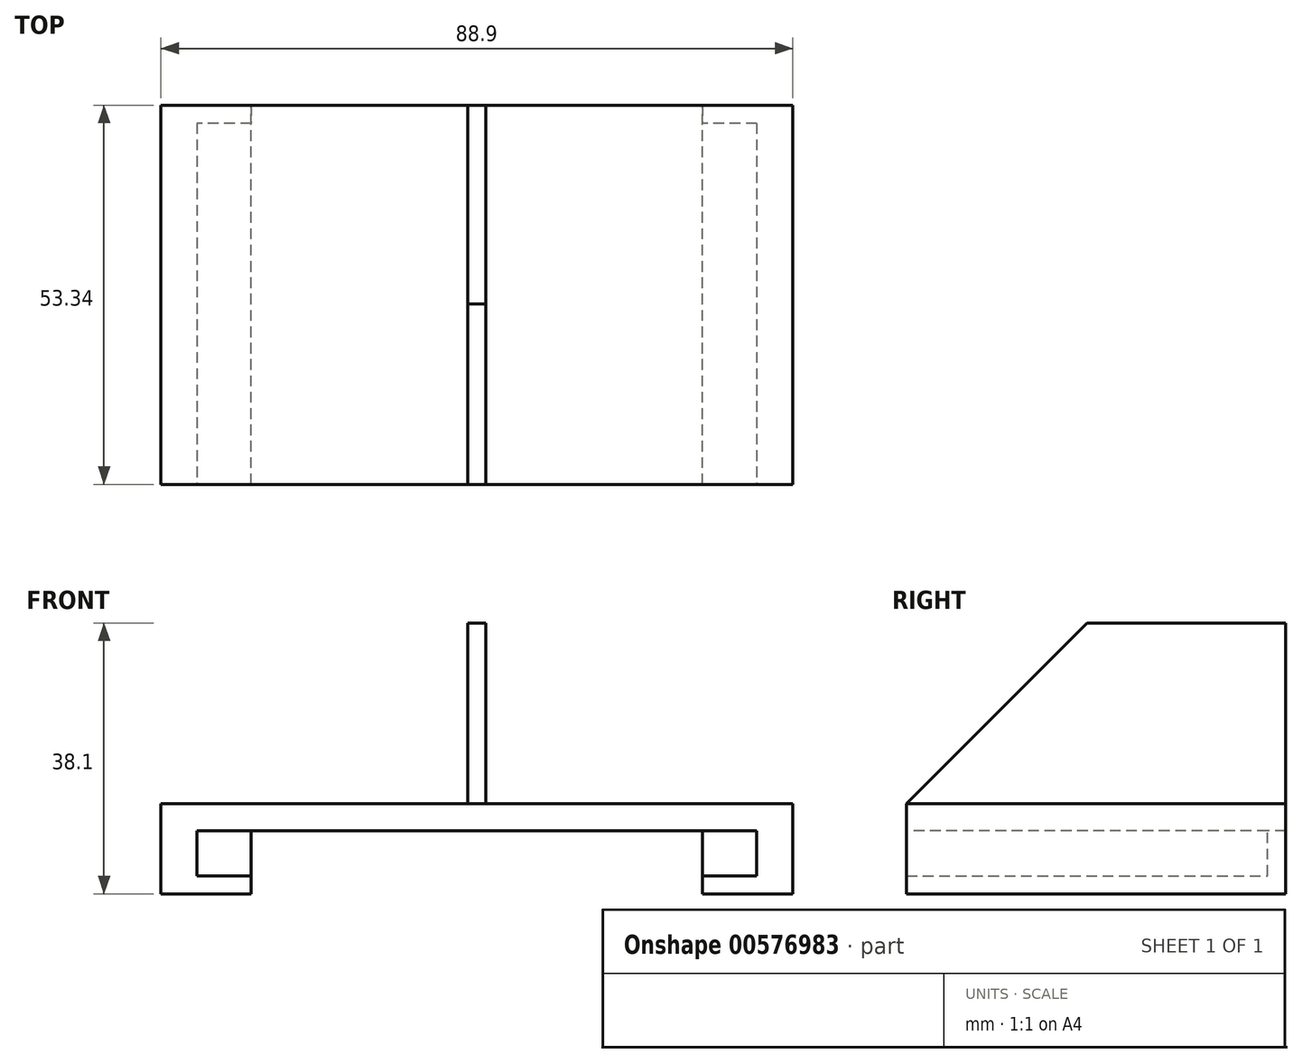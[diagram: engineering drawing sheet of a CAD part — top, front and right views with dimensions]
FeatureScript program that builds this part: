
annotation { "Feature Type Name" : "Feature", "Feature Type Description" : "" }
export const myFeature = defineFeature(function(context is Context, id is Id, definition is map)
    precondition{}
    {
        {
            var Q0;
            Q0=qCreatedBy(makeId("Top.planeOp"),FACE);
            var sketch = newSketch(context, id + "F0", { "sketchPlane" : qUnion([Q0])});
            skLineSegment(sketch, "E0.bottom", {"start": v(44.45, -26.67) * mm, "end": v(-44.45, -26.67) * mm});
            skLineSegment(sketch, "E0.top", {"start": v(44.45, 26.67) * mm, "end": v(-44.45, 26.67) * mm});
            skLineSegment(sketch, "E0.left", {"start": v(44.45, -26.67) * mm, "end": v(44.45, 26.67) * mm});
            skLineSegment(sketch, "E0.right", {"start": v(-44.45, -26.67) * mm, "end": v(-44.45, 26.67) * mm});
            skPoint(sketch, "E0.middle", {"position": v(0, 0) * mm});
            skSolve(sketch);
        }
        {
            var Q0;
            Q0=makeQuery(id+"F0.imprint","IMPRINT",FACE,{"disambiguationData":[TD([[makeQuery(id+"F0.imprint","IMPRINT",EDGE,{"derivedFrom":sQuery(id+"F0.wireOp",EDGE,"E0.bottom")}),-1.0]])]});
            extrude(context, id + "F1", {"entities" : qUnion([Q0]), "depth" : 12.7 * mm, "offsetDistance" : 25.4 * mm});
        }
        {
            var Q0;
            Q0=makeQuery(id+"F1.opExtrude","SWEPT_FACE",FACE,{"disambiguationData":[OSD([sQuery(id+"F0.wireOp",EDGE,"E0.bottom")])]});
            var sketch = newSketch(context, id + "F2", { "sketchPlane" : qUnion([Q0])});
            skLineSegment(sketch, "E1.bottom", {"start": v(39.37, 2.54) * mm, "end": v(-39.37, 2.54) * mm});
            skLineSegment(sketch, "E1.top", {"start": v(39.37, 8.9) * mm, "end": v(-39.37, 8.9) * mm});
            skLineSegment(sketch, "E1.left", {"start": v(39.37, 2.54) * mm, "end": v(39.37, 8.9) * mm});
            skLineSegment(sketch, "E1.right", {"start": v(-39.37, 2.54) * mm, "end": v(-39.37, 8.9) * mm});
            skPoint(sketch, "E1.middle", {"position": v(0, 5.72) * mm});
            skSolve(sketch);
        }
        {
            var Q0;
            Q0=makeQuery(id+"F2.imprint","IMPRINT",FACE,{"disambiguationData":[TD([[makeQuery(id+"F2.imprint","IMPRINT",EDGE,{"derivedFrom":sQuery(id+"F2.wireOp",EDGE,"E1.bottom")}),-1.0]])]});
            extrude(context, id + "F3", {"entities" : qUnion([Q0]), "operationType" : NewBodyOperationType.REMOVE, "oppositeDirection" : true, "depth" : 50.8 * mm, "offsetDistance" : 25.4 * mm});
        }
        {
            var Q0;
            Q0=makeQuery(id+"F1.opExtrude","SWEPT_FACE",FACE,{"disambiguationData":[OSD([sQuery(id+"F0.wireOp",EDGE,"E0.bottom")])]});
            var sketch = newSketch(context, id + "F4", { "sketchPlane" : qUnion([Q0])});
            skLineSegment(sketch, "E2.bottom", {"start": v(31.75, -8.9) * mm, "end": v(-31.75, -8.9) * mm});
            skLineSegment(sketch, "E2.top", {"start": v(31.75, 8.9) * mm, "end": v(-31.75, 8.9) * mm});
            skLineSegment(sketch, "E2.left", {"start": v(31.75, -8.9) * mm, "end": v(31.75, 8.9) * mm});
            skLineSegment(sketch, "E2.right", {"start": v(-31.75, -8.9) * mm, "end": v(-31.75, 8.9) * mm});
            skPoint(sketch, "E2.middle", {"position": v(0, 0) * mm});
            skSolve(sketch);
        }
        {
            var Q0;
            Q0 = qSketchRegion(id + "F4", true);
            extrude(context, id + "F5", {"entities" : qUnion([Q0]), "operationType" : NewBodyOperationType.REMOVE, "endBound" : BoundingType.THROUGH_ALL, "oppositeDirection" : true, "depth" : 25.4 * mm, "offsetDistance" : 25.4 * mm});
        }
        {
            var Q0;
            Q0=makeQuery(id+"F1.opExtrude","CAP_FACE",FACE,{"disambiguationData":[OSD([sQuery(id+"F0.wireOp",EDGE,"E0.bottom"),sQuery(id+"F0.wireOp",EDGE,"E0.top"),sQuery(id+"F0.wireOp",EDGE,"E0.left"),sQuery(id+"F0.wireOp",EDGE,"E0.right")])],"isStart":false});
            var sketch = newSketch(context, id + "F6", { "sketchPlane" : qUnion([Q0])});
            skLineSegment(sketch, "E3.bottom", {"start": v(1.27, -26.67) * mm, "end": v(-1.27, -26.67) * mm});
            skLineSegment(sketch, "E3.top", {"start": v(1.27, 26.67) * mm, "end": v(-1.27, 26.67) * mm});
            skLineSegment(sketch, "E3.left", {"start": v(1.27, -26.67) * mm, "end": v(1.27, 26.67) * mm});
            skLineSegment(sketch, "E3.right", {"start": v(-1.27, -26.67) * mm, "end": v(-1.27, 26.67) * mm});
            skPoint(sketch, "E3.middle", {"position": v(0, 0) * mm});
            skSolve(sketch);
        }
        {
            var Q0;
            Q0 = qSketchRegion(id + "F6", true);
            extrude(context, id + "F7", {"entities" : qUnion([Q0]), "operationType" : NewBodyOperationType.ADD, "depth" : 25.4 * mm, "offsetDistance" : 25.4 * mm});
        }
        {
            var Q0;
            Q0=makeQuery(id+"F7.opExtrude","CAP_EDGE",EDGE,{"disambiguationData":[OSD([sQuery(id+"F6.wireOp",EDGE,"E3.bottom")])],"isStart":false});
            chamfer(context, id + "F8", {"entities" : qUnion([Q0]), "width" : 25.4 * mm, "tangentPropagation" : true});
        }
    });
